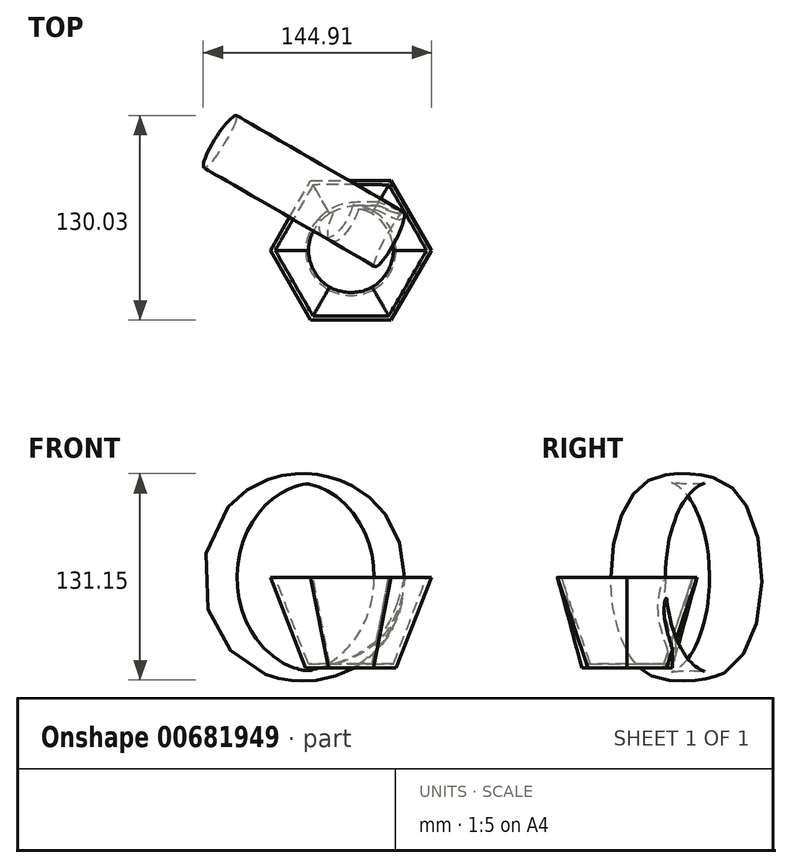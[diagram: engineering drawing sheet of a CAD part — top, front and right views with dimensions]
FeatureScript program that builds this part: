
annotation { "Feature Type Name" : "Feature", "Feature Type Description" : "" }
export const myFeature = defineFeature(function(context is Context, id is Id, definition is map)
    precondition{}
    {
        {
            var Q0;
            Q0=qCreatedBy(makeId("Top.planeOp"),FACE);
            var sketch = newSketch(context, id + "F0", { "sketchPlane" : qUnion([Q0])});
            skCircle(sketch, "E0", {"center": v(0, 0) * mm, "radius": 28.71 * mm});
            skSolve(sketch);
        }
        {
            var Q0;
            Q0=qCreatedBy(makeId("Top.planeOp"),FACE);
            cPlane(context, id + "F1", {"entities" : qUnion([Q0]), "cplaneType" : CPlaneType.OFFSET, "offset" : 57.4 * mm, "width" : 152.4 * mm, "height" : 152.4 * mm});
        }
        {
            var Q0;
            Q0=qCreatedBy(id+"F1.planeOp",FACE);
            var sketch = newSketch(context, id + "F2", { "sketchPlane" : qUnion([Q0])});
            skCircle(sketch, "E1.cCircle", {"center": v(0, 0) * mm, "radius": 44.3 * mm, "construction": true});
            skLineSegment(sketch, "E1.0", {"start": v(51.16, 0) * mm, "end": v(25.58, -44.31) * mm});
            skLineSegment(sketch, "E1.1", {"start": v(25.58, -44.31) * mm, "end": v(-25.59, -44.3) * mm});
            skLineSegment(sketch, "E1.2", {"start": v(-25.59, -44.3) * mm, "end": v(-51.16, 0) * mm});
            skLineSegment(sketch, "E1.3", {"start": v(-51.16, 0) * mm, "end": v(-25.58, 44.31) * mm});
            skLineSegment(sketch, "E1.4", {"start": v(-25.58, 44.31) * mm, "end": v(25.59, 44.3) * mm});
            skLineSegment(sketch, "E1.5", {"start": v(25.59, 44.3) * mm, "end": v(51.16, 0) * mm});
            skPoint(sketch, "E1.0.midPoint", {"position": v(38.37, -22.16) * mm});
            skSolve(sketch);
        }
        {
            var Q0;
            Q0=makeQuery(id+"F0.imprint","IMPRINT",FACE,{"disambiguationData":[TD([[makeQuery(id+"F0.imprint","IMPRINT",EDGE,{"derivedFrom":sQuery(id+"F0.wireOp",EDGE,"E0")}),1.0]])]});
            var Q1;
            Q1=makeQuery(id+"F2.imprint","IMPRINT",FACE,{"disambiguationData":[TD([[makeQuery(id+"F2.imprint","IMPRINT",EDGE,{"derivedFrom":sQuery(id+"F2.wireOp",EDGE,"E1.0")}),-1.0]])]});
            loft(context, id + "F3", {"sheetProfilesArray" : [{ "sheetProfileEntities" : qUnion([Q0]) }, { "sheetProfileEntities" : qUnion([Q1]) }]});
        }
        {
            var Q0;
            Q0=makeQuery(id+"F3.opLoft","CAP_FACE",FACE,{"disambiguationData":[OSD([makeQuery(id+"F2.imprint","IMPRINT",FACE,{"disambiguationData":[TD([[makeQuery(id+"F2.imprint","IMPRINT",EDGE,{"derivedFrom":sQuery(id+"F2.wireOp",EDGE,"E1.0")}),-1.0]])]})])],"isStart":true});
            shell(context, id + "F4", {"entities" : qUnion([Q0]), "thickness" : 2.54 * mm});
        }
        {
            var Q0;
            Q0=qCreatedBy(makeId("Top.planeOp"),FACE);
            var sketch = newSketch(context, id + "F5", { "sketchPlane" : qUnion([Q0])});
            skEllipse(sketch, "E2", {"center": v(-49.62, 49.74) * mm, "majorRadius": 19.65 * mm, "minorRadius": 8.62 * mm, "majorAxis": v(0.58, 0.81)});
            skSolve(sketch);
        }
        {
            var Q0;
            Q0=makeQuery(id+"F5.imprint","IMPRINT",FACE,{"disambiguationData":[TD([[makeQuery(id+"F5.imprint","IMPRINT",EDGE,{"derivedFrom":sQuery(id+"F5.wireOp",EDGE,"E2")}),1.0]])]});
            var Q1;
            Q1=makeQuery(id+"F3.opLoft","MID_CAP_EDGE",EDGE,{"disambiguationData":[OSD([sQuery(id+"F2.wireOp",EDGE,"E1.2"),sQuery(id+"F2.wireOp",EDGE,"E1.3"),sQuery(id+"F2.wireOp",EDGE,"E1.4")])],"capPos":1.0});
            revolve(context, id + "F6", {"operationType" : NewBodyOperationType.ADD, "entities" : qUnion([Q0]), "axis" : qUnion([Q1]), "revolveType" : RevolveType.FULL});
        }
    });
